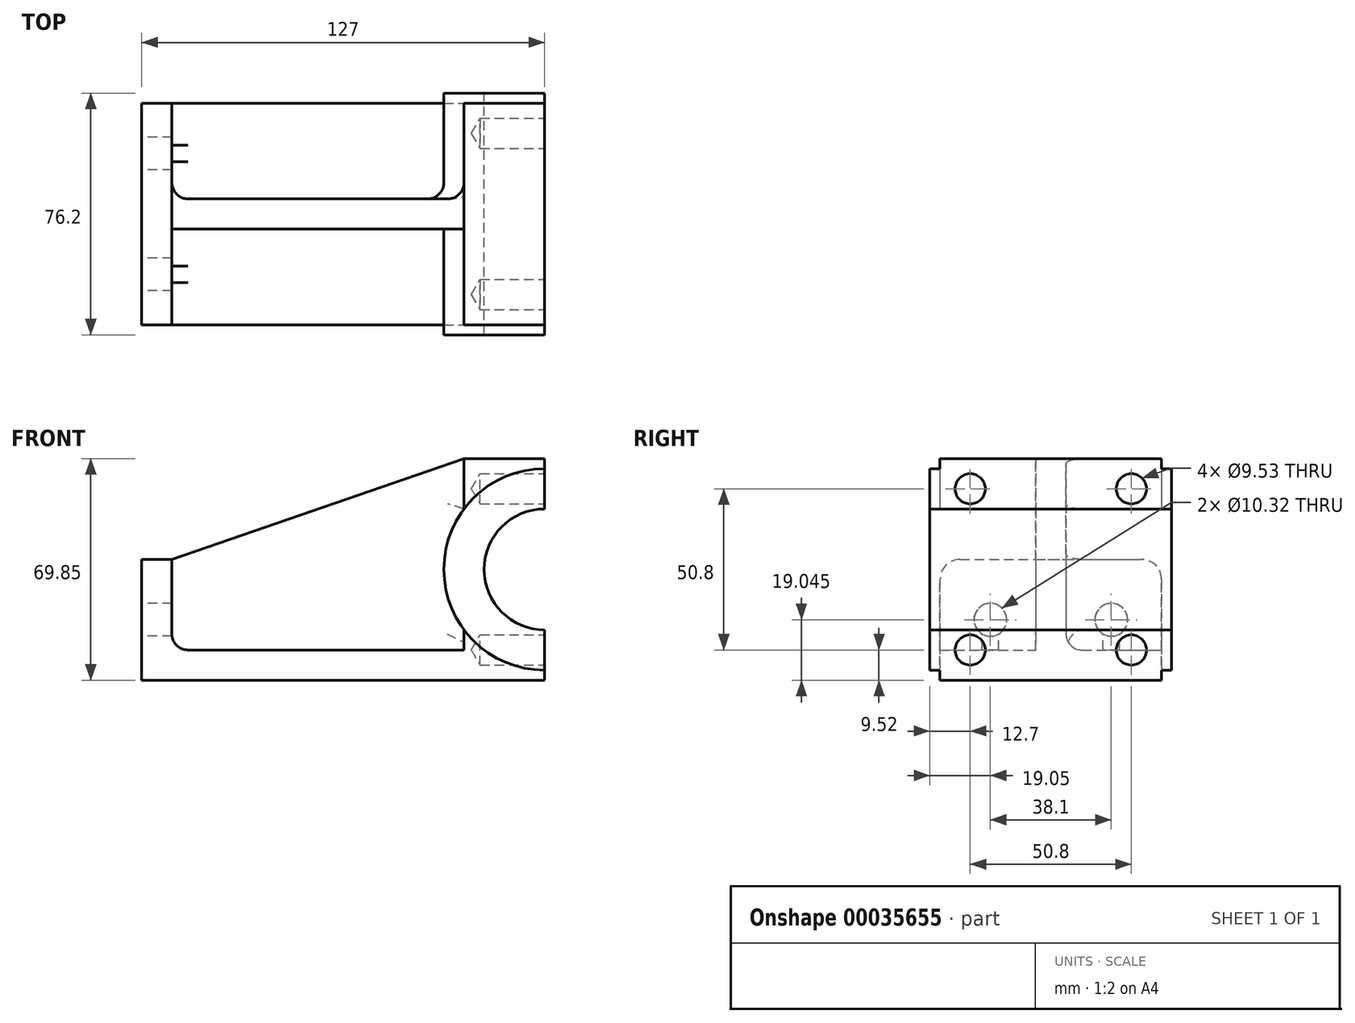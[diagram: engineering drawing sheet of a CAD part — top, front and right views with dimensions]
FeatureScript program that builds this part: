
annotation { "Feature Type Name" : "Feature", "Feature Type Description" : "" }
export const myFeature = defineFeature(function(context is Context, id is Id, definition is map)
    precondition{}
    {
        {
            var Q0;
            Q0=qCreatedBy(makeId("Front.planeOp"),FACE);
            var sketch = newSketch(context, id + "F0", { "sketchPlane" : qUnion([Q0])});
            skArc(sketch, "E0", {"start": v(0, 19.05) * mm, "mid": v(-19.05, 0) * mm, "end": v(0, -19.05) * mm});
            skArc(sketch, "E1", {"start": v(0, 31.75) * mm, "mid": v(-31.75, 0) * mm, "end": v(0, -31.75) * mm});
            skLineSegment(sketch, "E2", {"start": v(0, 31.75) * mm, "end": v(0, -31.75) * mm, "construction": true});
            skLineSegment(sketch, "E3", {"start": v(0, 31.75) * mm, "end": v(0, 19.05) * mm});
            skLineSegment(sketch, "E4", {"start": v(0, -19.05) * mm, "end": v(0, -31.75) * mm});
            skSolve(sketch);
        }
        {
            var Q0;
            Q0=makeQuery(id+"F0.imprint","IMPRINT",FACE,{"disambiguationData":[TD([[makeQuery(id+"F0.imprint","IMPRINT",EDGE,{"derivedFrom":sQuery(id+"F0.wireOp",EDGE,"E0")}),-1.0]])]});
            extrude(context, id + "F1", {"entities" : qUnion([Q0]), "endBound" : BoundingType.SYMMETRIC, "depth" : 76.2 * mm});
        }
        {
            var Q0;
            Q0=qCreatedBy(makeId("Front.planeOp"),FACE);
            var sketch = newSketch(context, id + "F2", { "sketchPlane" : qUnion([Q0])});
            skLineSegment(sketch, "E5", {"start": v(0, -34.92) * mm, "end": v(-127, -34.93) * mm});
            skLineSegment(sketch, "E6", {"start": v(-127, -34.93) * mm, "end": v(-127, 3.17) * mm});
            skLineSegment(sketch, "E7", {"start": v(-127, 3.17) * mm, "end": v(-117.47, 3.17) * mm});
            skLineSegment(sketch, "E8", {"start": v(-117.47, 3.17) * mm, "end": v(-117.47, -25.4) * mm});
            skLineSegment(sketch, "E9", {"start": v(-117.47, -25.4) * mm, "end": v(-25.4, -25.4) * mm});
            skArc(sketch, "E10.0", {"start": v(0, 31.75) * mm, "mid": v(-31.75, 0) * mm, "end": v(0, -31.75) * mm});
            skLineSegment(sketch, "E11", {"start": v(-25.4, -25.4) * mm, "end": v(-25.4, -19.05) * mm});
            skLineSegment(sketch, "E12", {"start": v(0, -34.92) * mm, "end": v(0, -31.75) * mm});
            skLineSegment(sketch, "E13", {"start": v(0, 31.75) * mm, "end": v(0, 34.92) * mm});
            skLineSegment(sketch, "E14", {"start": v(0, 34.92) * mm, "end": v(-25.4, 34.92) * mm});
            skLineSegment(sketch, "E15", {"start": v(-25.4, 34.92) * mm, "end": v(-25.4, 19.05) * mm});
            skSolve(sketch);
        }
        {
            var Q0;
            Q0 = qSketchRegion(id + "F2", true);
            extrude(context, id + "F3", {"entities" : qUnion([Q0]), "operationType" : NewBodyOperationType.ADD, "endBound" : BoundingType.SYMMETRIC, "depth" : 69.85 * mm});
        }
        {
            var Q0;
            Q0=qCreatedBy(makeId("Front.planeOp"),FACE);
            var sketch = newSketch(context, id + "F4", { "sketchPlane" : qUnion([Q0])});
            skLineSegment(sketch, "E16.0", {"start": v(-117.47, 3.17) * mm, "end": v(-117.47, -25.4) * mm});
            skLineSegment(sketch, "E17.0", {"start": v(-117.47, -25.4) * mm, "end": v(-25.4, -25.4) * mm});
            skArc(sketch, "E18.0", {"start": v(0, 31.75) * mm, "mid": v(-31.75, 0) * mm, "end": v(0, -31.75) * mm});
            skLineSegment(sketch, "E19.0", {"start": v(-25.4, 34.92) * mm, "end": v(-25.4, 19.05) * mm});
            skLineSegment(sketch, "E20", {"start": v(-117.47, 3.17) * mm, "end": v(-25.4, 34.93) * mm});
            skLineSegment(sketch, "E21.0", {"start": v(-25.4, -25.4) * mm, "end": v(-25.4, -19.05) * mm});
            skSolve(sketch);
        }
        {
            var Q0;
            Q0=makeQuery(id+"F4.imprint","IMPRINT",FACE,{"disambiguationData":[TD([[makeQuery(id+"F4.imprint","IMPRINT",EDGE,{"derivedFrom":sQuery(id+"F4.wireOp",EDGE,"E16.0")}),1.0]])]});
            extrude(context, id + "F5", {"entities" : qUnion([Q0]), "operationType" : NewBodyOperationType.ADD, "endBound" : BoundingType.SYMMETRIC, "depth" : 9.52 * mm});
        }
        {
            var Q0;
            Q0=makeQuery(id+"F3.boolean.opBoolean","MERGE",FACE,{"derivedFrom":[makeQuery(id+"F1.opExtrude","SWEPT_FACE",FACE,{"disambiguationData":[OSD([sQuery(id+"F0.wireOp",EDGE,"E3")])]}),makeQuery(id+"F3.opExtrude","SWEPT_FACE",FACE,{"disambiguationData":[OSD([sQuery(id+"F2.wireOp",EDGE,"E13")])]})]});
            var sketch = newSketch(context, id + "F6", { "sketchPlane" : qUnion([Q0])});
            skLineSegment(sketch, "E22.0", {"start": v(-34.93, 34.92) * mm, "end": v(34.93, 34.92) * mm});
            skLineSegment(sketch, "E23.bottom", {"start": v(-25.4, 25.4) * mm, "end": v(25.4, 25.4) * mm});
            skLineSegment(sketch, "E23.top", {"start": v(-25.4, -25.4) * mm, "end": v(25.4, -25.4) * mm});
            skLineSegment(sketch, "E23.left", {"start": v(-25.4, 25.4) * mm, "end": v(-25.4, -25.4) * mm});
            skLineSegment(sketch, "E23.right", {"start": v(25.4, 25.4) * mm, "end": v(25.4, -25.4) * mm});
            skLineSegment(sketch, "E24.0", {"start": v(-34.93, -34.92) * mm, "end": v(34.93, -34.92) * mm});
            skLineSegment(sketch, "E25", {"start": v(0, 34.92) * mm, "end": v(0, 25.4) * mm, "construction": true});
            skLineSegment(sketch, "E26", {"start": v(0, -25.4) * mm, "end": v(0, -34.92) * mm, "construction": true});
            skSolve(sketch);
        }
        {
            var Q0;
            Q0=sQuery(id+"F6.wireOp",VERTEX,"E23.left.start");
            var Q1;
            Q1=sQuery(id+"F6.wireOp",VERTEX,"E23.bottom.end");
            var Q2;
            Q2=sQuery(id+"F6.wireOp",VERTEX,"E23.top.end");
            var Q3;
            Q3=sQuery(id+"F6.wireOp",VERTEX,"E23.left.end");
            var Q4;
            Q4=makeQuery(id+"F1.opExtrude","SWEPT_BODY",BODY,{"disambiguationData":[OSD([sQuery(id+"F0.wireOp",EDGE,"E0"),sQuery(id+"F0.wireOp",EDGE,"E1"),sQuery(id+"F0.wireOp",EDGE,"E3"),sQuery(id+"F0.wireOp",EDGE,"E4")])]});
            hole(context, id + "F7", {"style" : HoleStyle.SIMPLE, "holeDiameter" : 9.52 * mm, "endStyle" : HoleEndStyle.BLIND, "holeDepth" : 20.32 * mm, "locations" : qUnion([Q0, Q1, Q2, Q3]), "scope" : qUnion([Q4])});
        }
        {
            var Q0;
            Q0=makeQuery(id+"F3.opExtrude","SWEPT_FACE",FACE,{"disambiguationData":[OSD([sQuery(id+"F2.wireOp",EDGE,"E6")])]});
            var sketch = newSketch(context, id + "F8", { "sketchPlane" : qUnion([Q0])});
            skLineSegment(sketch, "E27", {"start": v(0, -34.93) * mm, "end": v(0, -15.88) * mm, "construction": true});
            skPoint(sketch, "E27.endSnap0", {"position": v(0, -34.93) * mm});
            skLineSegment(sketch, "E28.0", {"start": v(34.93, -34.93) * mm, "end": v(34.93, 3.17) * mm});
            skLineSegment(sketch, "E29", {"start": v(-19.05, -15.88) * mm, "end": v(19.05, -15.88) * mm});
            skSolve(sketch);
        }
        {
            var Q0;
            Q0=sQuery(id+"F8.wireOp",VERTEX,"E29.start");
            var Q1;
            Q1=sQuery(id+"F8.wireOp",VERTEX,"E29.end");
            var Q2;
            Q2=makeQuery(id+"F1.opExtrude","SWEPT_BODY",BODY,{"disambiguationData":[OSD([sQuery(id+"F0.wireOp",EDGE,"E0"),sQuery(id+"F0.wireOp",EDGE,"E1"),sQuery(id+"F0.wireOp",EDGE,"E3"),sQuery(id+"F0.wireOp",EDGE,"E4")])]});
            hole(context, id + "F9", {"style" : HoleStyle.SIMPLE, "holeDiameter" : 10.32 * mm, "endStyle" : HoleEndStyle.BLIND, "holeDepth" : 38.1 * mm, "locations" : qUnion([Q0, Q1]), "scope" : qUnion([Q2])});
        }
        {
            var Q0;
            {var subQ0=sQuery(id+"F2.wireOp",EDGE,"E10.0");Q0=makeQuery(id+"F3.opExtrude","CAP_EDGE",EDGE,{"disambiguationData":[OSD([subQ0]),TDD([makeQuery(id+"F2.imprint","IMPRINT",EDGE,{"disambiguationData":[TD([[makeQuery(id+"F2.imprint","INTERSECT",VERTEX,{"derivedFrom":[subQ0,sQuery(id+"F2.wireOp",EDGE,"E12")]}),1.0]])],"derivedFrom":subQ0})])],"isStart":false});}
            var Q1;
            {var subQ0=sQuery(id+"F2.wireOp",EDGE,"E10.0");Q1=makeQuery(id+"F3.opExtrude","CAP_EDGE",EDGE,{"disambiguationData":[OSD([subQ0]),TDD([makeQuery(id+"F2.imprint","IMPRINT",EDGE,{"disambiguationData":[TD([[makeQuery(id+"F2.imprint","INTERSECT",VERTEX,{"derivedFrom":[subQ0,sQuery(id+"F2.wireOp",EDGE,"E13")]}),-1.0]])],"derivedFrom":subQ0})])],"isStart":false});}
            var Q2;
            {var subQ0=sQuery(id+"F2.wireOp",EDGE,"E10.0");Q2=makeQuery(id+"F3.opExtrude","CAP_EDGE",EDGE,{"disambiguationData":[OSD([subQ0]),TDD([makeQuery(id+"F2.imprint","IMPRINT",EDGE,{"disambiguationData":[TD([[makeQuery(id+"F2.imprint","INTERSECT",VERTEX,{"derivedFrom":[subQ0,sQuery(id+"F2.wireOp",EDGE,"E13")]}),-1.0]])],"derivedFrom":subQ0})])],"isStart":true});}
            var Q3;
            {var subQ0=sQuery(id+"F2.wireOp",EDGE,"E10.0");Q3=makeQuery(id+"F3.opExtrude","CAP_EDGE",EDGE,{"disambiguationData":[OSD([subQ0]),TDD([makeQuery(id+"F2.imprint","IMPRINT",EDGE,{"disambiguationData":[TD([[makeQuery(id+"F2.imprint","INTERSECT",VERTEX,{"derivedFrom":[subQ0,sQuery(id+"F2.wireOp",EDGE,"E12")]}),1.0]])],"derivedFrom":subQ0})])],"isStart":true});}
            var Q4;
            {var subQ0=sQuery(id+"F2.wireOp",EDGE,"E8");var subQ1=sQuery(id+"F2.wireOp",EDGE,"E9");Q4=makeQuery(id+"F5.boolean.opBoolean","SPLIT",EDGE,{"disambiguationData":[TD([makeQuery(id+"F5.opExtrude","CAP_FACE",FACE,{"disambiguationData":[OSD([sQuery(id+"F4.wireOp",EDGE,"E16.0"),sQuery(id+"F4.wireOp",EDGE,"E17.0"),sQuery(id+"F4.wireOp",EDGE,"E18.0"),sQuery(id+"F4.wireOp",EDGE,"E19.0"),sQuery(id+"F4.wireOp",EDGE,"E20"),sQuery(id+"F4.wireOp",EDGE,"E21.0")])],"isStart":false})])],"derivedFrom":makeQuery(id+"F3.opExtrude","SWEPT_EDGE",EDGE,{"disambiguationData":[OSD([subQ0,subQ1])]})});}
            var Q5;
            Q5=makeQuery(id+"F5.opExtrude","CAP_EDGE",EDGE,{"disambiguationData":[OSD([sQuery(id+"F4.wireOp",EDGE,"E16.0")])],"isStart":false});
            var Q6;
            Q6=makeQuery(id+"F5.opExtrude","CAP_EDGE",EDGE,{"disambiguationData":[OSD([sQuery(id+"F4.wireOp",EDGE,"E17.0")])],"isStart":false});
            var Q7;
            Q7=makeQuery(id+"F5.opExtrude","CAP_EDGE",EDGE,{"disambiguationData":[OSD([sQuery(id+"F4.wireOp",EDGE,"E17.0")])],"isStart":true});
            var Q8;
            Q8=makeQuery(id+"F5.opExtrude","CAP_EDGE",EDGE,{"disambiguationData":[OSD([sQuery(id+"F4.wireOp",EDGE,"E16.0")])],"isStart":true});
            var Q9;
            {var subQ0=sQuery(id+"F2.wireOp",EDGE,"E8");var subQ1=sQuery(id+"F2.wireOp",EDGE,"E9");Q9=makeQuery(id+"F5.boolean.opBoolean","SPLIT",EDGE,{"disambiguationData":[TD([makeQuery(id+"F5.opExtrude","CAP_FACE",FACE,{"disambiguationData":[OSD([sQuery(id+"F4.wireOp",EDGE,"E16.0"),sQuery(id+"F4.wireOp",EDGE,"E17.0"),sQuery(id+"F4.wireOp",EDGE,"E18.0"),sQuery(id+"F4.wireOp",EDGE,"E19.0"),sQuery(id+"F4.wireOp",EDGE,"E20"),sQuery(id+"F4.wireOp",EDGE,"E21.0")])],"isStart":true})])],"derivedFrom":makeQuery(id+"F3.opExtrude","SWEPT_EDGE",EDGE,{"disambiguationData":[OSD([subQ0,subQ1])]})});}
            var Q10;
            Q10=makeQuery(id+"F5.opExtrude","CAP_EDGE",EDGE,{"disambiguationData":[OSD([sQuery(id+"F4.wireOp",EDGE,"E21.0")])],"isStart":true});
            var Q11;
            Q11=makeQuery(id+"F5.opExtrude","CAP_EDGE",EDGE,{"disambiguationData":[OSD([sQuery(id+"F4.wireOp",EDGE,"E18.0")])],"isStart":true});
            var Q12;
            Q12=makeQuery(id+"F5.opExtrude","CAP_EDGE",EDGE,{"disambiguationData":[OSD([sQuery(id+"F4.wireOp",EDGE,"E19.0")])],"isStart":true});
            var Q13;
            Q13=makeQuery(id+"F5.opExtrude","CAP_EDGE",EDGE,{"disambiguationData":[OSD([sQuery(id+"F4.wireOp",EDGE,"E21.0")])],"isStart":false});
            var Q14;
            Q14=makeQuery(id+"F5.opExtrude","CAP_EDGE",EDGE,{"disambiguationData":[OSD([sQuery(id+"F4.wireOp",EDGE,"E18.0")])],"isStart":false});
            var Q15;
            Q15=makeQuery(id+"F5.opExtrude","CAP_EDGE",EDGE,{"disambiguationData":[OSD([sQuery(id+"F4.wireOp",EDGE,"E19.0")])],"isStart":false});
            fillet(context, id + "F10", {"entities" : qUnion([Q0, Q1, Q2, Q3, Q4, Q5, Q6, Q7, Q8, Q9, Q10, Q11, Q12, Q13, Q14, Q15]), "radius" : 5.08 * mm, "tangentPropagation" : true, "allowEdgeOverflow" : false});
        }
        {
            var Q0;
            Q0=makeQuery(id+"F3.opExtrude","CAP_EDGE",EDGE,{"disambiguationData":[OSD([sQuery(id+"F2.wireOp",EDGE,"E7")])],"isStart":true});
            var Q1;
            Q1=makeQuery(id+"F3.opExtrude","CAP_EDGE",EDGE,{"disambiguationData":[OSD([sQuery(id+"F2.wireOp",EDGE,"E7")])],"isStart":false});
            fillet(context, id + "F11", {"entities" : qUnion([Q0, Q1]), "radius" : 6.35 * mm, "tangentPropagation" : true, "allowEdgeOverflow" : false});
        }
    });
